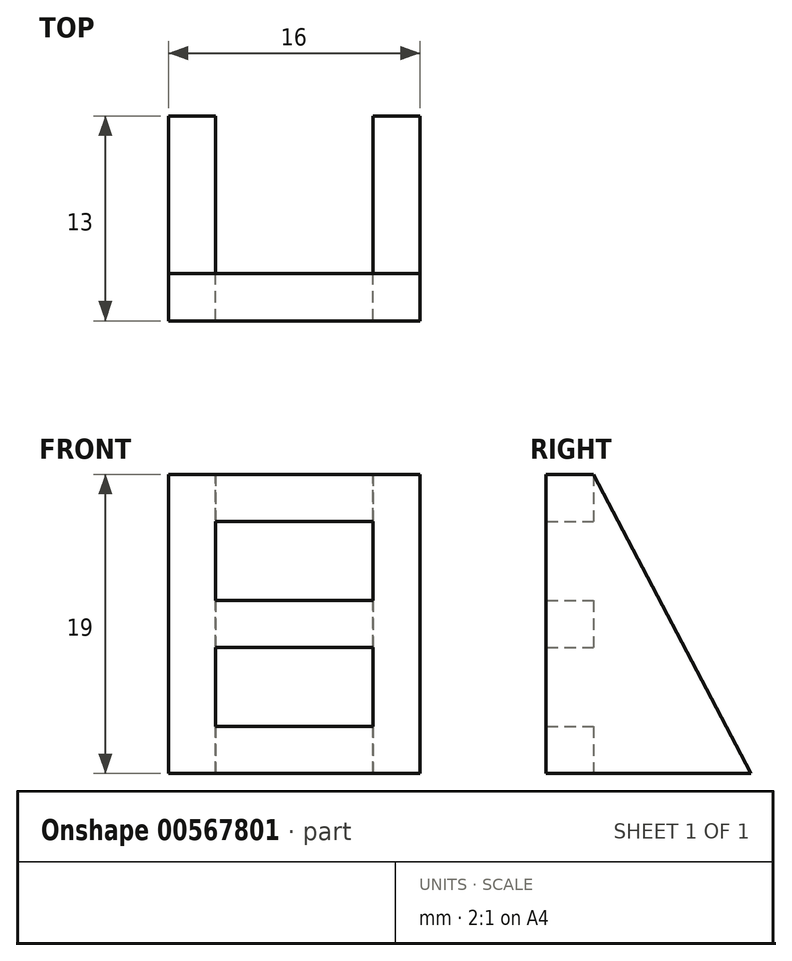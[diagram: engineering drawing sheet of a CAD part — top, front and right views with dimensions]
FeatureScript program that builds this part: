
annotation { "Feature Type Name" : "Feature", "Feature Type Description" : "" }
export const myFeature = defineFeature(function(context is Context, id is Id, definition is map)
    precondition{}
    {
        {
            var Q0;
            Q0=qCreatedBy(makeId("Front.planeOp"),FACE);
            var sketch = newSketch(context, id + "F0", { "sketchPlane" : qUnion([Q0])});
            skLineSegment(sketch, "E0.bottom", {"start": v(8, 5.5) * mm, "end": v(-8, 5.5) * mm});
            skLineSegment(sketch, "E0.top", {"start": v(5, -5.5) * mm, "end": v(-5, -5.5) * mm});
            skLineSegment(sketch, "E0.left", {"start": v(8, 5.5) * mm, "end": v(8, -5.5) * mm});
            skLineSegment(sketch, "E0.right", {"start": v(-8, 5.5) * mm, "end": v(-8, -5.5) * mm});
            skPoint(sketch, "E0.middle", {"position": v(0, 0) * mm});
            skLineSegment(sketch, "E1.bottom", {"start": v(5, 2.5) * mm, "end": v(-5, 2.5) * mm});
            skLineSegment(sketch, "E1.top", {"start": v(5, -2.5) * mm, "end": v(-5, -2.5) * mm});
            skLineSegment(sketch, "E1.left", {"start": v(5, 2.5) * mm, "end": v(5, -2.5) * mm});
            skLineSegment(sketch, "E1.right", {"start": v(-5, 2.5) * mm, "end": v(-5, -2.5) * mm});
            skLineSegment(sketch, "E2", {"start": v(-8, -5.5) * mm, "end": v(-8, -13.5) * mm});
            skLineSegment(sketch, "E3", {"start": v(-8, -13.5) * mm, "end": v(8, -13.5) * mm});
            skLineSegment(sketch, "E4", {"start": v(8, -13.5) * mm, "end": v(8, -5.5) * mm});
            skLineSegment(sketch, "E5", {"start": v(-5, -5.5) * mm, "end": v(-5, -10.5) * mm});
            skLineSegment(sketch, "E6", {"start": v(-5, -10.5) * mm, "end": v(5, -10.5) * mm});
            skLineSegment(sketch, "E7", {"start": v(5, -10.5) * mm, "end": v(5, -5.5) * mm});
            skSolve(sketch);
        }
        {
            var Q0;
            Q0=makeQuery(id+"F0.imprint","IMPRINT",FACE,{"disambiguationData":[TD([[makeQuery(id+"F0.imprint","IMPRINT",EDGE,{"derivedFrom":sQuery(id+"F0.wireOp",EDGE,"E0.bottom")}),1.0]])]});
            extrude(context, id + "F1", {"entities" : qUnion([Q0]), "depth" : 3 * mm, "offsetDistance" : 25 * mm});
        }
        {
            var Q0;
            Q0=qCreatedBy(makeId("Right.planeOp"),FACE);
            var sketch = newSketch(context, id + "F2", { "sketchPlane" : qUnion([Q0])});
            skPoint(sketch, "E8.0", {"position": v(0, 5.5) * mm});
            skPoint(sketch, "E8.1", {"position": v(0, -13.5) * mm});
            skLineSegment(sketch, "E9", {"start": v(0, 5.5) * mm, "end": v(0, -13.5) * mm});
            skLineSegment(sketch, "E10", {"start": v(10, -13.5) * mm, "end": v(0, 5.5) * mm});
            skLineSegment(sketch, "E11", {"start": v(0, -13.5) * mm, "end": v(10, -13.5) * mm});
            skSolve(sketch);
        }
        {
            var Q0;
            Q0=makeQuery(id+"F2.imprint","IMPRINT",FACE,{"disambiguationData":[TD([[makeQuery(id+"F2.imprint","IMPRINT",EDGE,{"derivedFrom":sQuery(id+"F2.wireOp",EDGE,"E9")}),1.0]])]});
            extrude(context, id + "F3", {"entities" : qUnion([Q0]), "operationType" : NewBodyOperationType.ADD, "endBound" : BoundingType.SYMMETRIC, "depth" : 16 * mm, "offsetDistance" : 25 * mm});
        }
        {
            var Q0;
            Q0 = qSketchRegion(id + "F2", true);
            extrude(context, id + "F4", {"entities" : qUnion([Q0]), "operationType" : NewBodyOperationType.REMOVE, "endBound" : BoundingType.SYMMETRIC, "oppositeDirection" : true, "depth" : 10 * mm, "offsetDistance" : 25 * mm});
        }
    });
